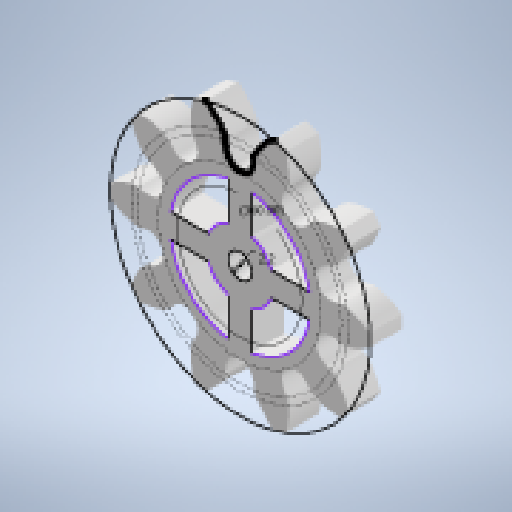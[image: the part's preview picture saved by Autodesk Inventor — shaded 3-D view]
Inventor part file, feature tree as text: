
AUTODESK INVENTOR PART (.ipt)
format: ipt  version: 2023 (Build 270158000, 158)  size: 267,776 bytes
history: native  units: mm
features: extrude x4, other x1, sketch x1, pattern_circular x1
ambient origin geometry x8: Origin, YZ Plane, XZ Plane, XY Plane, X Axis, Y Axis, Z Axis, Center Point
bodies: Solid1 (feature_tree)
feature tree (7):
  other  "pinion_V6"
  sketch  "Sketch1"  dims[d0=3.0mm d1=0.0mm d2=2.2mm d3=2.0mm d4=1.0mm d9=0.0mm d10=0.0mm d11=0.0mm d12=0.0mm d13=100.0mm d14=360.0deg d16=6.5mm d17=1.6mm d18=0.0mm]
  extrude  "Extrusion1"  Depth=1.6mm
  extrude  "Extrusion2"  Depth=1.6mm
  extrude  "Extrusion3"  TaperAngle=0.0deg  [1 undecoded]
  pattern_circular  "Circular Pattern1"  [2 undecoded]
  extrude  "Extrusion4"  Depth=1.6mm TaperAngle=360.0deg
note: 3 required parameter values undecoded (feature->parameter linkage not recoverable at this tier; creation-order binding heuristic only, values carry confidence <= 0.55)
